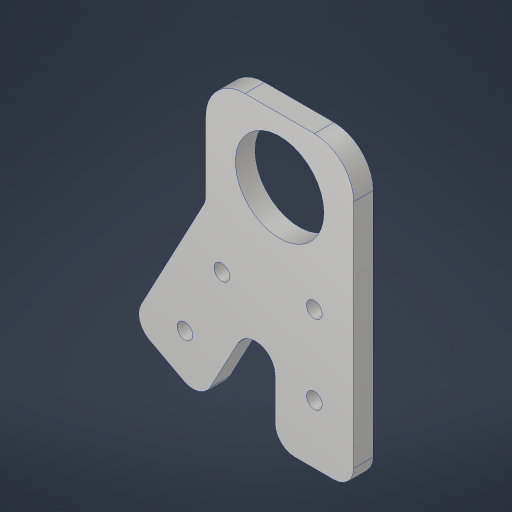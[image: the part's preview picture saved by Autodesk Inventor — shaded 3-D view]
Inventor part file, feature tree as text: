
AUTODESK INVENTOR PART (.ipt)
format: ipt  version: 2023.4 (Build 274418000, 418)  size: 245,760 bytes
history: native  units: in
note: dims shown in document units (in); Inventor stores cm internally (conversion verified against a paired STEP export)
features: projected_geometry x3, sketch x2, extrude x2, hole x2, fillet x2
ambient origin geometry x8: Origin, YZ Plane, XZ Plane, XY Plane, X Axis, Y Axis, Z Axis, Center Point
bodies: Solid1 (feature_tree)
feature tree (11):
  sketch  "Sketch1"  dims[d0=1.0in d1=1.0in]
  extrude  "Extrusion1"  Depth=1.0in
  hole  "Hole1"  [1 undecoded]
  sketch  "Sketch2"  dims[d2=0.1924in d3=2.0in d4=1.0in d5=0.5in d6=1.0in d7=0.5in d8=2.25in d9=0.25in d10=0.0in d11=0.201in d12=0.75in d13=0.385in d14=0.25in d15=0.5635in d16=1.0in d17=0.8108in d18=0.25in d19=1.125in d20=0.625in d21=0.25in d22=1.0in d23=0.0in d24=1.125in d25=0.75in d26=0.385in d27=0.25in d28=0.5635in d29=1.0in d30=0.8108in d31=0.5in]
  extrude  "Extrusion2"  Depth=1.0in
  hole  "Hole2"  [1 undecoded]
  fillet  "Fillet1"  Radius=1.0in
  fillet  "Fillet2"  Radius=0.5in
  projected_geometry  "Projected Loop1"
  projected_geometry  "Project Cut Edges1"
  projected_geometry  "Project Cut Edges2"
note: 2 required parameter values undecoded (feature->parameter linkage not recoverable at this tier; creation-order binding heuristic only, values carry confidence <= 0.55)
